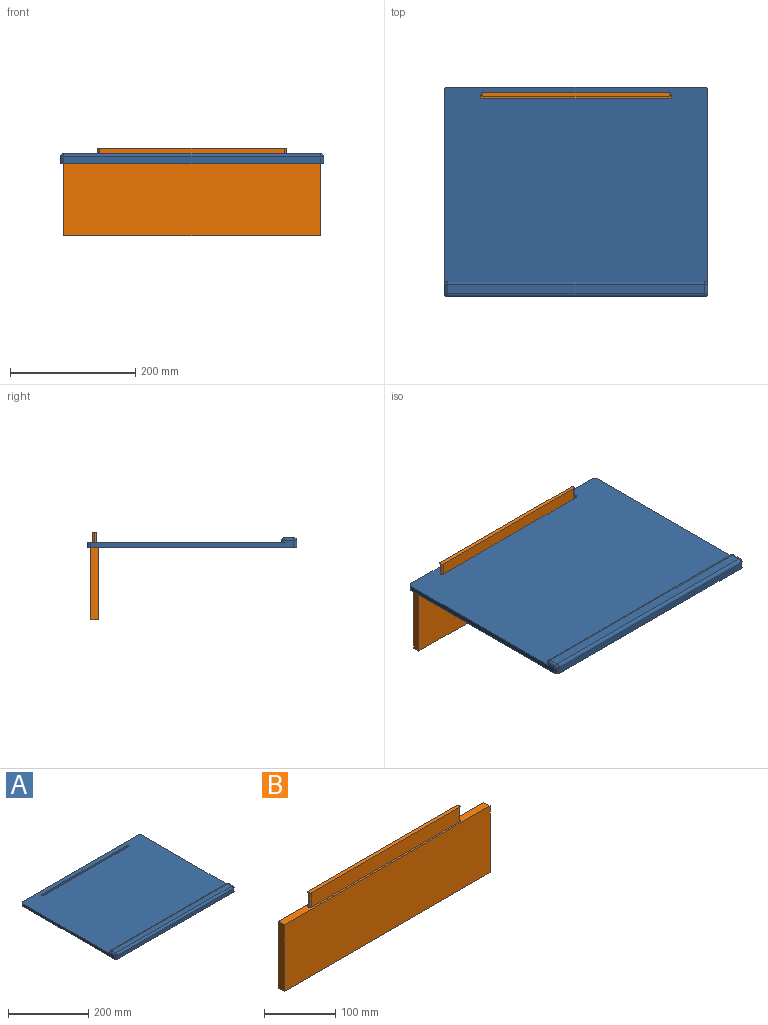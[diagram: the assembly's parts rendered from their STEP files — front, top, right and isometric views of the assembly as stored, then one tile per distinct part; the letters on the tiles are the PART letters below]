
ASSEMBLY  parts=2 mates=1
PART A: 26 faces, bbox 420x335x16 mm
  f0: plane 420x315mm, normal (0,0,1), area 128371.7mm2, adj f1,f3,f4,f6,f10,f11,f12,f13
  f1: plane 325x11mm, normal (-1,0,0), area 2645mm2, adj f0,f5,f14,f16,f18,f25
  f2: plane 410x11mm, normal (0,-1,0), area 4510mm2, adj f5,f9,f14,f19
  f3: plane 325x11mm, normal (1,0,0), area 2645mm2, adj f0,f5,f19,f21,f23,f24
  f4: plane 410x8mm, normal (0,1,0), area 3280mm2, adj f0,f5,f24,f25
  f5: plane 420x335mm, normal (0,0,-1), area 138850.3mm2, adj f1,f2,f3,f4,f10,f11,f12,f13
  f6: plane 410x3mm, normal (0,1,0), area 1230mm2, adj f0,f7,f18,f23
  f7: cylinder r=5mm len=410mm, axis (1,0,0), area 3220.1mm2, adj f6,f8,f17,f22
  f8: plane 410x15mm, normal (0,0,1), area 6150mm2, adj f7,f9,f16,f21
  f9: cylinder r=5mm len=410mm, axis (1,0,0), area 3220.1mm2, adj f2,f8,f15,f20
  f10: plane 300x8mm, normal (0,1,0), area 2400mm2, adj f0,f5,f11,f13
  f11: cylinder r=3mm len=8mm, axis (0,0,1), area 75.4mm2, adj f0,f5,f10,f12
  f12: plane 300x8mm, normal (0,-1,0), area 2400mm2, adj f0,f5,f11,f13
  f13: cylinder r=3mm len=8mm, axis (0,0,1), area 75.4mm2, adj f0,f5,f10,f12
  f14: cylinder r=5mm len=11mm, axis (0,0,1), area 86.4mm2, adj f1,f2,f5,f15
  f15: sphere r=5mm, area 39.3mm2, adj f9,f14,f16
  f16: cylinder r=5mm len=15mm, axis (0,-1,0), area 117.8mm2, adj f1,f8,f15,f17
  f17: sphere r=5mm, area 39.3mm2, adj f7,f16,f18
  f18: cylinder r=5mm len=5mm, axis (0,0,1), area 23.6mm2, adj f0,f1,f6,f17
  f19: cylinder r=5mm len=11mm, axis (0,0,-1), area 86.4mm2, adj f2,f3,f5,f20
  f20: sphere r=5mm, area 39.3mm2, adj f9,f19,f21
  f21: cylinder r=5mm len=15mm, axis (0,1,0), area 117.8mm2, adj f3,f8,f20,f22
  f22: sphere r=5mm, area 39.3mm2, adj f7,f21,f23
  f23: cylinder r=5mm len=5mm, axis (0,0,-1), area 23.6mm2, adj f0,f3,f6,f22
  f24: cylinder r=5mm len=8mm, axis (0,0,1), area 62.8mm2, adj f0,f3,f4,f5
  f25: cylinder r=5mm len=8mm, axis (0,0,-1), area 62.8mm2, adj f0,f1,f4,f5
PART B: 15 faces, bbox 410x12x140 mm
  f0: plane 410x12mm, normal (0,0,1), area 3125.4mm2, adj f1,f3,f4,f5,f6,f8,f9,f10
  f1: plane 115x12mm, normal (1,0,0), area 1380mm2, adj f0,f2,f4,f5
  f2: plane 410x12mm, normal (0,0,-1), area 4920mm2, adj f1,f3,f4,f5
  f3: plane 115x12mm, normal (-1,0,0), area 1380mm2, adj f0,f2,f4,f5
  f4: plane 410x115mm, normal (0,1,0), area 47150mm2, adj f0,f1,f2,f3
  f5: plane 410x115mm, normal (0,-1,0), area 47150mm2, adj f0,f1,f2,f3
  f6: plane 25x1mm, normal (-1,0,0), area 25mm2, adj f0,f7,f11,f13
  f7: plane 300x6mm, normal (0,0,1), area 1794.6mm2, adj f6,f8,f9,f10,f11,f12,f13,f14
  f8: plane 25x1mm, normal (1,0,0), area 25mm2, adj f0,f7,f12,f14
  f9: plane 295x25mm, normal (0,1,0), area 7375mm2, adj f0,f7,f13,f14
  f10: plane 295x25mm, normal (0,-1,0), area 7375mm2, adj f0,f7,f11,f12
  f11: cylinder r=2.5mm len=25mm, axis (0,0,1), area 98.2mm2, adj f0,f6,f7,f10
  f12: cylinder r=2.5mm len=25mm, axis (0,0,-1), area 98.2mm2, adj f0,f7,f8,f10
  f13: cylinder r=2.5mm len=25mm, axis (0,0,-1), area 98.2mm2, adj f0,f6,f7,f9
  f14: cylinder r=2.5mm len=25mm, axis (0,0,1), area 98.2mm2, adj f0,f7,f8,f9
PLACE A t=(-71.46,-104.57,-76.72)mm
PLACE B t=(-71.46,-116.57,-76.72)mm
MATE fastened B.f0 <-> A.f5  axis (0,0,1) through (78.54,68.43,-76.72)mm
